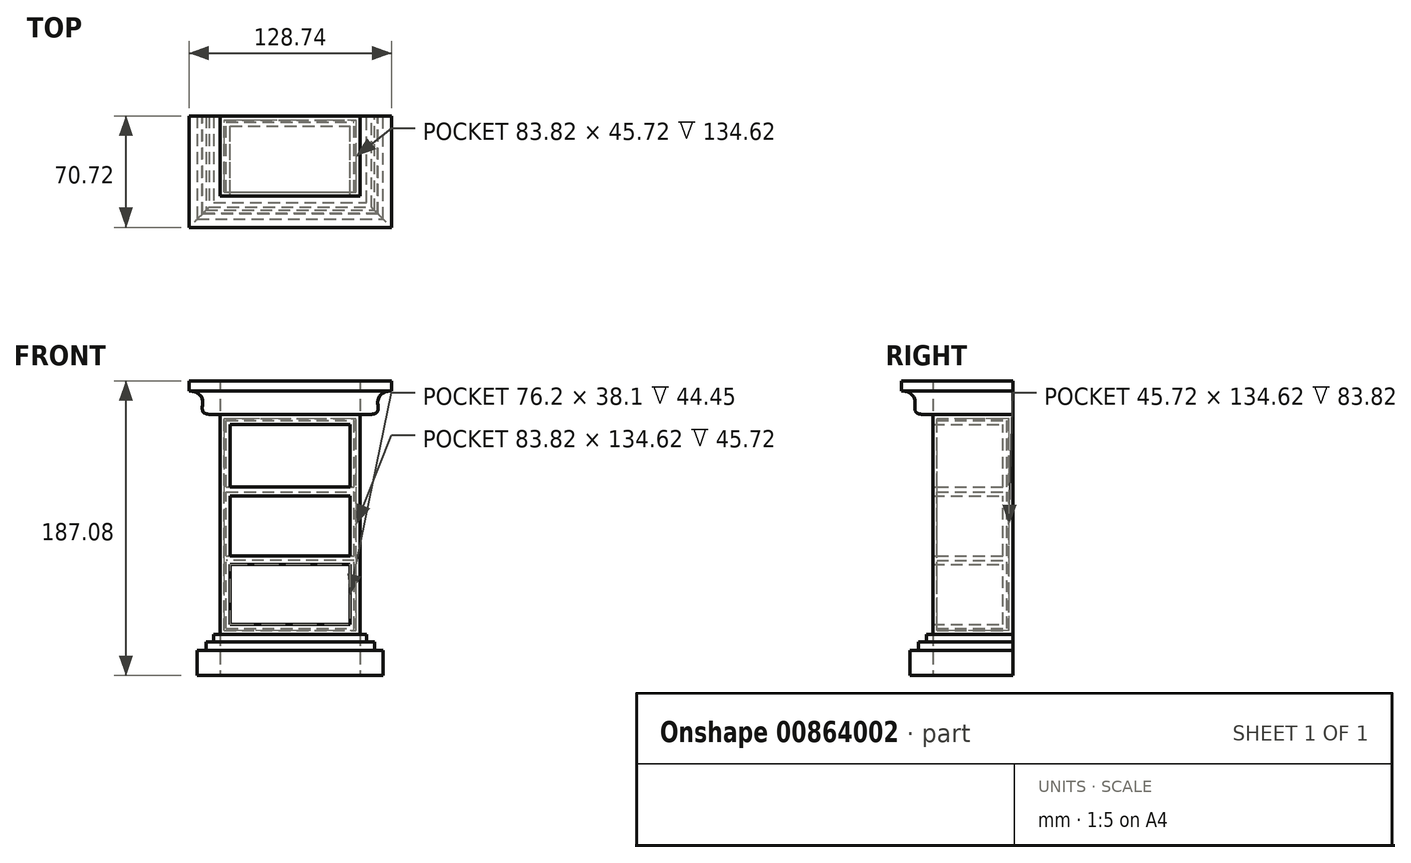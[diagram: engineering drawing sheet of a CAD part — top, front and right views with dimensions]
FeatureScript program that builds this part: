
annotation { "Feature Type Name" : "Feature", "Feature Type Description" : "" }
export const myFeature = defineFeature(function(context is Context, id is Id, definition is map)
    precondition{}
    {
        {
            var Q0;
            Q0=qCreatedBy(makeId("Front.planeOp"),FACE);
            var sketch = newSketch(context, id + "F0", { "sketchPlane" : qUnion([Q0])});
            skLineSegment(sketch, "E0.bottom", {"start": v(0, 0) * mm, "end": v(88.9, 0) * mm});
            skLineSegment(sketch, "E0.top", {"start": v(0, 139.7) * mm, "end": v(88.9, 139.7) * mm});
            skLineSegment(sketch, "E0.left", {"start": v(0, 0) * mm, "end": v(0, 139.7) * mm});
            skLineSegment(sketch, "E0.right", {"start": v(88.9, 0) * mm, "end": v(88.9, 139.7) * mm});
            skSolve(sketch);
        }
        {
            var Q0;
            Q0=makeQuery(id+"F0.imprint","IMPRINT",FACE,{"disambiguationData":[TD([[makeQuery(id+"F0.imprint","IMPRINT",EDGE,{"derivedFrom":sQuery(id+"F0.wireOp",EDGE,"E0.bottom")}),1.0]])]});
            extrude(context, id + "F1", {"entities" : qUnion([Q0]), "depth" : 50.8 * mm, "offsetDistance" : 25.4 * mm});
        }
        {
            var Q0;
            Q0=makeQuery(id+"F1.opExtrude","CAP_FACE",FACE,{"disambiguationData":[OSD([sQuery(id+"F0.wireOp",EDGE,"E0.bottom"),sQuery(id+"F0.wireOp",EDGE,"E0.top"),sQuery(id+"F0.wireOp",EDGE,"E0.left"),sQuery(id+"F0.wireOp",EDGE,"E0.right")])],"isStart":false});
            shell(context, id + "F2", {"entities" : qUnion([Q0]), "thickness" : 6.35 * mm});
        }
        {
            var Q0;
            Q0=makeQuery(id+"F1.opExtrude","SWEPT_FACE",FACE,{"disambiguationData":[OSD([sQuery(id+"F0.wireOp",EDGE,"E0.top")])]});
            var sketch = newSketch(context, id + "F3", { "sketchPlane" : qUnion([Q0])});
            skLineSegment(sketch, "E1", {"start": v(0, 0) * mm, "end": v(0, -50.8) * mm});
            skLineSegment(sketch, "E2", {"start": v(0, -50.8) * mm, "end": v(88.9, -50.8) * mm});
            skLineSegment(sketch, "E3", {"start": v(88.9, -50.8) * mm, "end": v(88.9, 0) * mm});
            skSolve(sketch);
        }
        {
            var Q0;
            Q0=makeQuery(id+"F1.opExtrude","CAP_FACE",FACE,{"disambiguationData":[OSD([sQuery(id+"F0.wireOp",EDGE,"E0.bottom"),sQuery(id+"F0.wireOp",EDGE,"E0.top"),sQuery(id+"F0.wireOp",EDGE,"E0.left"),sQuery(id+"F0.wireOp",EDGE,"E0.right")])],"isStart":true});
            var sketch = newSketch(context, id + "F4", { "sketchPlane" : qUnion([Q0])});
            skLineSegment(sketch, "E4", {"start": v(0, 139.7) * mm, "end": v(0, 160.95) * mm});
            skLineSegment(sketch, "E5", {"start": v(0, 160.95) * mm, "end": v(19.92, 160.95) * mm});
            skLineSegment(sketch, "E6", {"start": v(19.92, 160.95) * mm, "end": v(19.92, 154.46) * mm});
            skLineSegment(sketch, "E7", {"start": v(0, 139.7) * mm, "end": v(7.12, 139.7) * mm});
            skPoint(sketch, "E8.0.internal.orphan", {"position": v(21.92, 154.46) * mm});
            skPoint(sketch, "E8.4.internal.orphan", {"position": v(8.94, 139.7) * mm});
            skFitSpline(sketch, "E9", {"points": [v(19.92, 154.46) * mm, v(11.4, 149.33) * mm, v(11.4, 143.17) * mm, v(7.12, 139.7) * mm], "startDerivative": vector(-36.52, 2.36) * mm, "endDerivative": vector(-33, -4.5) * mm});
            skSolve(sketch);
        }
        {
            var Q0;
            Q0=makeQuery(id+"F4.imprint","IMPRINT",FACE,{"disambiguationData":[TD([[makeQuery(id+"F4.imprint","IMPRINT",EDGE,{"derivedFrom":sQuery(id+"F4.wireOp",EDGE,"E4")}),-1.0]])]});
            var Q1;
            Q1=sQuery(id+"F3.wireOp",EDGE,"E1");
            var Q2;
            Q2=sQuery(id+"F3.wireOp",EDGE,"E2");
            var Q3;
            Q3=sQuery(id+"F3.wireOp",EDGE,"E3");
            sweep(context, id + "F5", {"profiles" : qUnion([Q0]), "path" : qUnion([Q1, Q2, Q3])});
        }
        {
            var Q0;
            Q0=makeQuery(id+"F1.opExtrude","SWEPT_FACE",FACE,{"disambiguationData":[OSD([sQuery(id+"F0.wireOp",EDGE,"E0.bottom")])]});
            var sketch = newSketch(context, id + "F6", { "sketchPlane" : qUnion([Q0])});
            skLineSegment(sketch, "E10", {"start": v(0, 0) * mm, "end": v(0, 50.8) * mm});
            skLineSegment(sketch, "E11", {"start": v(0, 50.8) * mm, "end": v(88.9, 50.8) * mm});
            skLineSegment(sketch, "E12", {"start": v(88.9, 50.8) * mm, "end": v(88.9, 0) * mm});
            skSolve(sketch);
        }
        {
            var Q0;
            Q0=makeQuery(id+"F1.opExtrude","CAP_FACE",FACE,{"disambiguationData":[OSD([sQuery(id+"F0.wireOp",EDGE,"E0.bottom"),sQuery(id+"F0.wireOp",EDGE,"E0.top"),sQuery(id+"F0.wireOp",EDGE,"E0.left"),sQuery(id+"F0.wireOp",EDGE,"E0.right")])],"isStart":true});
            var sketch = newSketch(context, id + "F7", { "sketchPlane" : qUnion([Q0])});
            skLineSegment(sketch, "E13.bottom", {"start": v(0, 0) * mm, "end": v(4.08, 0) * mm});
            skLineSegment(sketch, "E13.left", {"start": v(0, 0) * mm, "end": v(0, -26.13) * mm});
            skLineSegment(sketch, "E13.right", {"start": v(14.55, -10.31) * mm, "end": v(14.55, -26.13) * mm});
            skLineSegment(sketch, "E14", {"start": v(4.08, 0) * mm, "end": v(4.08, -4.73) * mm});
            skLineSegment(sketch, "E15", {"start": v(4.08, -4.73) * mm, "end": v(9, -4.73) * mm});
            skLineSegment(sketch, "E16", {"start": v(9, -4.73) * mm, "end": v(9, -10.31) * mm});
            skLineSegment(sketch, "E17", {"start": v(9, -10.31) * mm, "end": v(14.55, -10.31) * mm});
            skLineSegment(sketch, "E18", {"start": v(14.55, -10.31) * mm, "end": v(14.55, -14.43) * mm});
            skLineSegment(sketch, "E19", {"start": v(14.55, -14.43) * mm, "end": v(14.55, -26.13) * mm});
            skLineSegment(sketch, "E20", {"start": v(14.55, -26.13) * mm, "end": v(0, -26.13) * mm});
            skSolve(sketch);
        }
        {
            var Q0;
            Q0=makeQuery(id+"F7.imprint","IMPRINT",FACE,{"disambiguationData":[TD([[makeQuery(id+"F7.imprint","IMPRINT",EDGE,{"derivedFrom":sQuery(id+"F7.wireOp",EDGE,"E13.left")}),1.0]])]});
            var Q1;
            Q1=sQuery(id+"F6.wireOp",EDGE,"E12");
            var Q2;
            Q2=sQuery(id+"F6.wireOp",EDGE,"E10");
            var Q3;
            Q3=sQuery(id+"F6.wireOp",EDGE,"E11");
            sweep(context, id + "F8", {"profiles" : qUnion([Q0]), "path" : qUnion([Q1, Q2, Q3])});
        }
        {
            var Q0;
            Q0=makeQuery(id+"F2.opShell","OFFSET_FACE",FACE,{"disambiguationData":[OSD([sQuery(id+"F0.wireOp",EDGE,"E0.bottom"),sQuery(id+"F0.wireOp",EDGE,"E0.top"),sQuery(id+"F0.wireOp",EDGE,"E0.left"),sQuery(id+"F0.wireOp",EDGE,"E0.right")])]});
            var sketch = newSketch(context, id + "F9", { "sketchPlane" : qUnion([Q0])});
            skLineSegment(sketch, "E21", {"start": v(6.35, 93.74) * mm, "end": v(82.55, 93.74) * mm});
            skLineSegment(sketch, "E22", {"start": v(6.35, 87.93) * mm, "end": v(82.55, 87.93) * mm});
            skLineSegment(sketch, "E23", {"start": v(6.35, 87.93) * mm, "end": v(6.35, 93.74) * mm});
            skLineSegment(sketch, "E24", {"start": v(82.55, 87.93) * mm, "end": v(82.55, 93.74) * mm});
            skLineSegment(sketch, "E25", {"start": v(6.35, 49.83) * mm, "end": v(82.55, 49.83) * mm});
            skLineSegment(sketch, "E26", {"start": v(82.55, 49.83) * mm, "end": v(82.55, 44.45) * mm});
            skLineSegment(sketch, "E27", {"start": v(82.55, 44.45) * mm, "end": v(6.35, 44.45) * mm});
            skLineSegment(sketch, "E28", {"start": v(6.35, 44.45) * mm, "end": v(6.35, 49.83) * mm});
            skSolve(sketch);
        }
        {
            var Q0;
            Q0=makeQuery(id+"F9.imprint","IMPRINT",FACE,{"disambiguationData":[TD([[makeQuery(id+"F9.imprint","IMPRINT",EDGE,{"derivedFrom":sQuery(id+"F9.wireOp",EDGE,"E21")}),-1.0]])]});
            var Q1;
            Q1=makeQuery(id+"F9.imprint","IMPRINT",FACE,{"disambiguationData":[TD([[makeQuery(id+"F9.imprint","IMPRINT",EDGE,{"derivedFrom":sQuery(id+"F9.wireOp",EDGE,"E25")}),-1.0]])]});
            extrude(context, id + "F10", {"entities" : qUnion([Q0, Q1]), "operationType" : NewBodyOperationType.ADD, "depth" : 44.45 * mm, "offsetDistance" : 25.4 * mm});
        }
        {
            var Q0;
            Q0=makeQuery(id+"F10.opExtrude","SWEPT_FACE",FACE,{"disambiguationData":[OSD([sQuery(id+"F9.wireOp",EDGE,"E21")])]});
            var Q1;
            Q1=makeQuery(id+"F10.opExtrude","SWEPT_FACE",FACE,{"disambiguationData":[OSD([sQuery(id+"F9.wireOp",EDGE,"E25")])]});
            shell(context, id + "F11", {"entities" : qUnion([Q0, Q1]), "thickness" : 2.54 * mm});
        }
    });
